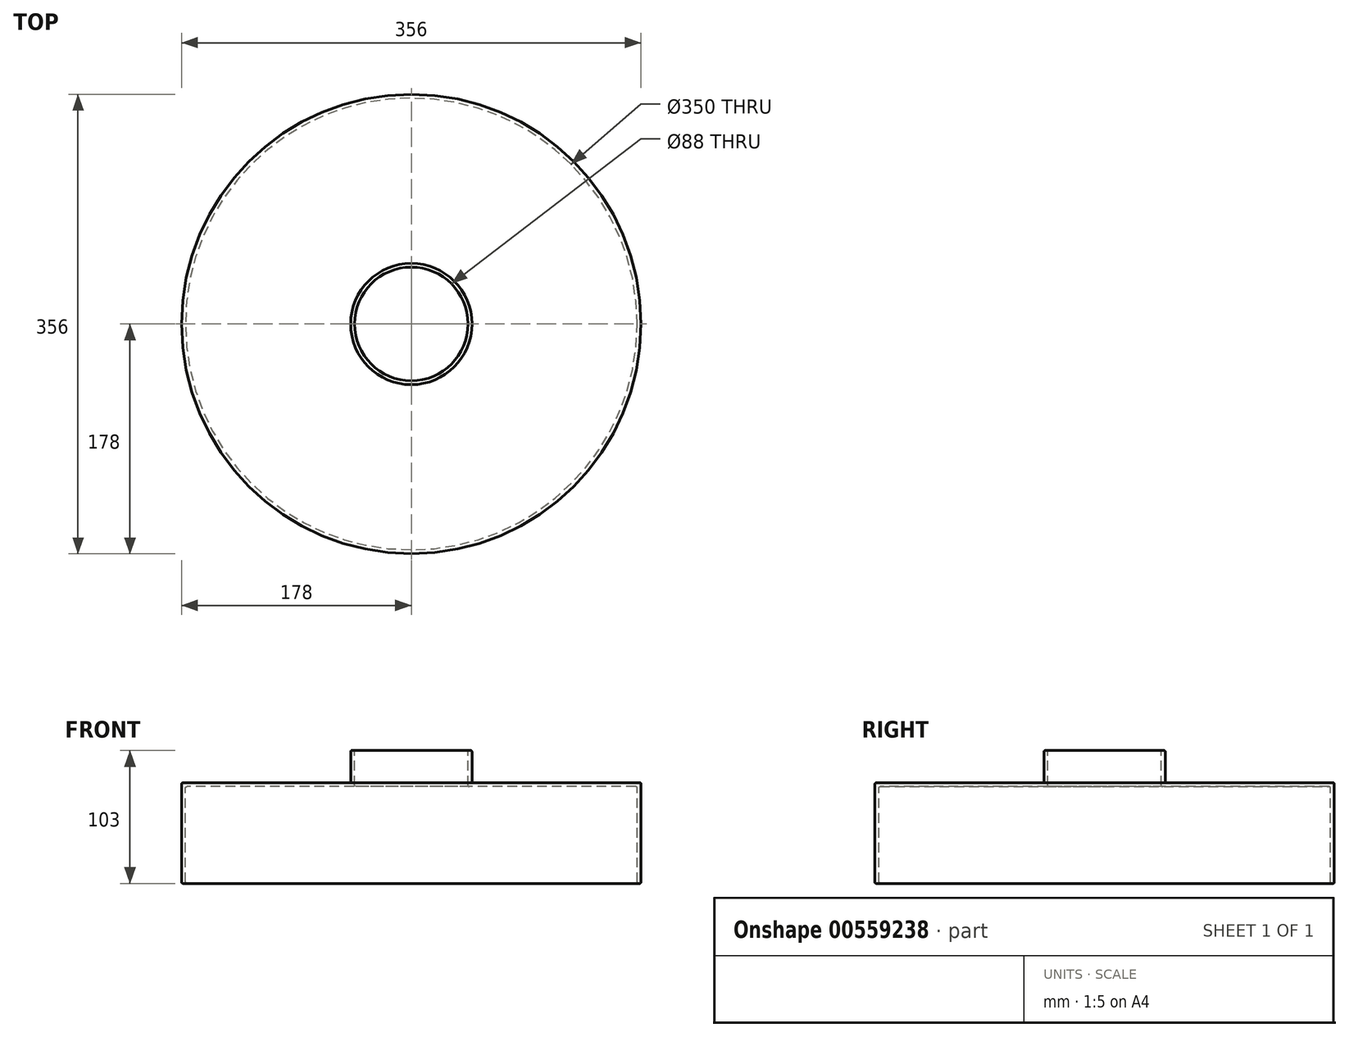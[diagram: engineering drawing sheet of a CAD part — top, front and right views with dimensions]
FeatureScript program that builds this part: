
annotation { "Feature Type Name" : "Feature", "Feature Type Description" : "" }
export const myFeature = defineFeature(function(context is Context, id is Id, definition is map)
    precondition{}
    {
        {
            var Q0;
            Q0=qCreatedBy(makeId("Right.planeOp"),FACE);
            var sketch = newSketch(context, id + "F0", { "sketchPlane" : qUnion([Q0])});
            skLineSegment(sketch, "E0.bottom", {"start": v(-177, 0) * mm, "end": v(-48, 0) * mm});
            skLineSegment(sketch, "E0.left", {"start": v(-178, -1) * mm, "end": v(-178, -77) * mm});
            skLineSegment(sketch, "E0.right", {"start": v(178, -1) * mm, "end": v(178, -77) * mm});
            skLineSegment(sketch, "E1.0", {"start": v(-174, -3) * mm, "end": v(-45, -3) * mm});
            skLineSegment(sketch, "E2.0", {"start": v(-175, -4) * mm, "end": v(-175, -77) * mm});
            skLineSegment(sketch, "E3.0", {"start": v(175, -4) * mm, "end": v(175, -77) * mm});
            skLineSegment(sketch, "E4", {"start": v(-177, -78) * mm, "end": v(-176, -78) * mm});
            skLineSegment(sketch, "E5", {"start": v(177, -78) * mm, "end": v(176, -78) * mm});
            skLineSegment(sketch, "E6", {"start": v(-44, -1) * mm, "end": v(-44, -2) * mm});
            skLineSegment(sketch, "E7", {"start": v(44, -1) * mm, "end": v(44, -2) * mm});
            skLineSegment(sketch, "E8", {"start": v(0, 0) * mm, "end": v(0, -82.28) * mm, "construction": true});
            skLineSegment(sketch, "E9.trimOffspring", {"start": v(45, -3) * mm, "end": v(174, -3) * mm});
            skLineSegment(sketch, "E10.trimOffspring", {"start": v(48, 0) * mm, "end": v(177, 0) * mm});
            skPoint(sketch, "E11.visualSharp", {"position": v(-178, 0) * mm});
            skArc(sketch, "E11.filletArc", {"start": v(-177, 0) * mm, "mid": v(-177.7, -0.3) * mm, "end": v(-178, -1) * mm});
            skPoint(sketch, "E12.visualSharp", {"position": v(-175, -3) * mm});
            skArc(sketch, "E12.filletArc", {"start": v(-174, -3) * mm, "mid": v(-174.7, -3.3) * mm, "end": v(-175, -4) * mm});
            skPoint(sketch, "E13.visualSharp", {"position": v(-44, 0) * mm});
            skPoint(sketch, "E14.visualSharp", {"position": v(-44, -3) * mm});
            skPoint(sketch, "E15.visualSharp", {"position": v(44, -3) * mm});
            skArc(sketch, "E15.filletArc", {"start": v(44, -2) * mm, "mid": v(44.3, -2.7) * mm, "end": v(45, -3) * mm});
            skPoint(sketch, "E16.visualSharp", {"position": v(44, 0) * mm});
            skPoint(sketch, "E17.visualSharp", {"position": v(178, 0) * mm});
            skArc(sketch, "E17.filletArc", {"start": v(178, -1) * mm, "mid": v(177.7, -0.3) * mm, "end": v(177, 0) * mm});
            skPoint(sketch, "E18.visualSharp", {"position": v(175, -3) * mm});
            skArc(sketch, "E18.filletArc", {"start": v(175, -4) * mm, "mid": v(174.7, -3.3) * mm, "end": v(174, -3) * mm});
            skPoint(sketch, "E19.visualSharp", {"position": v(178, -78) * mm});
            skArc(sketch, "E19.filletArc", {"start": v(177, -78) * mm, "mid": v(177.7, -77.7) * mm, "end": v(178, -77) * mm});
            skPoint(sketch, "E20.visualSharp", {"position": v(175, -78) * mm});
            skArc(sketch, "E20.filletArc", {"start": v(175, -77) * mm, "mid": v(175.3, -77.7) * mm, "end": v(176, -78) * mm});
            skPoint(sketch, "E21.visualSharp", {"position": v(-175, -78) * mm});
            skArc(sketch, "E21.filletArc", {"start": v(-176, -78) * mm, "mid": v(-175.3, -77.7) * mm, "end": v(-175, -77) * mm});
            skPoint(sketch, "E22.visualSharp", {"position": v(-178, -78) * mm});
            skArc(sketch, "E22.filletArc", {"start": v(-178, -77) * mm, "mid": v(-177.7, -77.7) * mm, "end": v(-177, -78) * mm});
            skLineSegment(sketch, "E23.bottom", {"start": v(-45, -3) * mm, "end": v(-47, -3) * mm});
            skLineSegment(sketch, "E23.top", {"start": v(-45, 25) * mm, "end": v(-46, 25) * mm});
            skLineSegment(sketch, "E23.left", {"start": v(-44, -2) * mm, "end": v(-44, -2) * mm});
            skLineSegment(sketch, "E23.right", {"start": v(-47, 1) * mm, "end": v(-47, 24) * mm});
            skLineSegment(sketch, "E24.trimOffspring", {"start": v(-44, -1) * mm, "end": v(-44, 24) * mm});
            skArc(sketch, "E25.filletArc", {"start": v(-45, -3) * mm, "mid": v(-44.3, -2.7) * mm, "end": v(-44, -2) * mm});
            skPoint(sketch, "E26.visualSharp", {"position": v(-47, 0) * mm});
            skArc(sketch, "E26.filletArc", {"start": v(-48, 0) * mm, "mid": v(-47.3, 0.3) * mm, "end": v(-47, 1) * mm});
            skPoint(sketch, "E27.visualSharp", {"position": v(-47, 25) * mm});
            skArc(sketch, "E27.filletArc", {"start": v(-46, 25) * mm, "mid": v(-46.7, 24.7) * mm, "end": v(-47, 24) * mm});
            skPoint(sketch, "E28.visualSharp", {"position": v(-44, 25) * mm});
            skArc(sketch, "E28.filletArc", {"start": v(-44, 24) * mm, "mid": v(-44.3, 24.7) * mm, "end": v(-45, 25) * mm});
            skLineSegment(sketch, "E29.bottom", {"start": v(45, -3) * mm, "end": v(47, -3) * mm});
            skLineSegment(sketch, "E29.top", {"start": v(45, 25) * mm, "end": v(46, 25) * mm});
            skLineSegment(sketch, "E29.left", {"start": v(44, -2) * mm, "end": v(44, 24) * mm});
            skLineSegment(sketch, "E29.right", {"start": v(47, 1) * mm, "end": v(47, 24) * mm});
            skPoint(sketch, "E30.visualSharp", {"position": v(44, 25) * mm});
            skArc(sketch, "E30.filletArc", {"start": v(45, 25) * mm, "mid": v(44.3, 24.7) * mm, "end": v(44, 24) * mm});
            skPoint(sketch, "E31.visualSharp", {"position": v(47, 25) * mm});
            skArc(sketch, "E31.filletArc", {"start": v(47, 24) * mm, "mid": v(46.7, 24.7) * mm, "end": v(46, 25) * mm});
            skArc(sketch, "E32.filletArc", {"start": v(47, 1) * mm, "mid": v(47.3, 0.3) * mm, "end": v(48, 0) * mm});
            skSolve(sketch);
        }
        {
            var Q0;
            Q0=makeQuery(id+"F0.imprint","IMPRINT",FACE,{"disambiguationData":[TD([[makeQuery(id+"F0.imprint","IMPRINT",EDGE,{"derivedFrom":sQuery(id+"F0.wireOp",EDGE,"E0.bottom")}),-1.0]])]});
            var Q1;
            Q1=sQuery(id+"F0.wireOp",EDGE,"E8");
            revolve(context, id + "F1", {"entities" : qUnion([Q0]), "axis" : qUnion([Q1]), "revolveType" : RevolveType.FULL});
        }
    });
